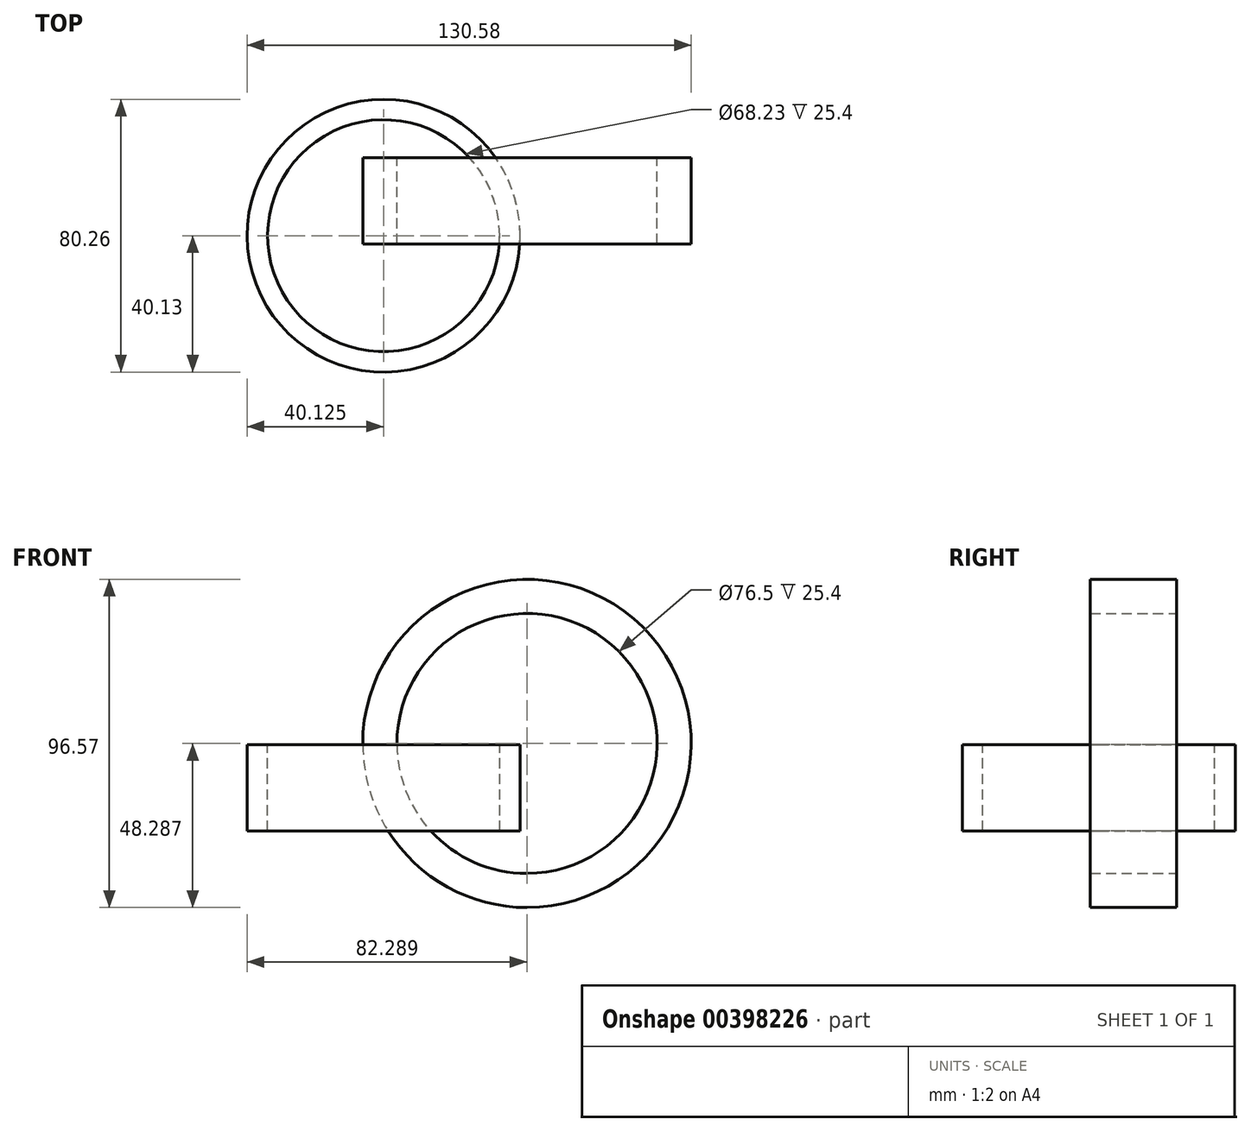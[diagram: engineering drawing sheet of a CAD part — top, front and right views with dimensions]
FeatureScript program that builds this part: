
annotation { "Feature Type Name" : "Feature", "Feature Type Description" : "" }
export const myFeature = defineFeature(function(context is Context, id is Id, definition is map)
    precondition{}
    {
        {
            var Q0;
            Q0=qCreatedBy(makeId("Top.planeOp"),FACE);
            var sketch = newSketch(context, id + "F0", { "sketchPlane" : qUnion([Q0])});
            skCircle(sketch, "E0", {"center": v(-59.1, 59.6) * mm, "radius": 40.13 * mm});
            skSolve(sketch);
        }
        {
            var Q0;
            Q0 = qSketchRegion(id + "F0", true);
            extrude(context, id + "F1", {"entities" : qUnion([Q0]), "depth" : 25.4 * mm});
        }
        {
            var Q0;
            Q0=makeQuery(id+"F1.opExtrude","CAP_FACE",FACE,{"disambiguationData":[OSD([sQuery(id+"F0.wireOp",EDGE,"E0")])],"isStart":false});
            var sketch = newSketch(context, id + "F2", { "sketchPlane" : qUnion([Q0])});
            skCircle(sketch, "E1", {"center": v(-59.1, 59.6) * mm, "radius": 34.12 * mm});
            skSolve(sketch);
        }
        {
            var Q0;
            Q0 = qSketchRegion(id + "F2", true);
            extrude(context, id + "F3", {"entities" : qUnion([Q0]), "operationType" : NewBodyOperationType.REMOVE, "endBound" : BoundingType.THROUGH_ALL, "oppositeDirection" : true, "depth" : 25.4 * mm});
        }
        {
            var Q0;
            Q0=qCreatedBy(makeId("Front.planeOp"),FACE);
            var sketch = newSketch(context, id + "F4", { "sketchPlane" : qUnion([Q0])});
            skCircle(sketch, "E2", {"center": v(-16.94, 25.75) * mm, "radius": 48.29 * mm});
            skCircle(sketch, "E3", {"center": v(-16.94, 25.75) * mm, "radius": 38.25 * mm});
            skSolve(sketch);
        }
        {
            var Q0;
            Q0 = qSketchRegion(id + "F4", true);
            extrude(context, id + "F5", {"entities" : qUnion([Q0]), "depth" : 25.4 * mm});
        }
        {
            var Q0;
            Q0=makeQuery(id+"F5.opExtrude","SWEPT_BODY",BODY,{"disambiguationData":[OSD([sQuery(id+"F4.wireOp",EDGE,"E2"),sQuery(id+"F4.wireOp",EDGE,"E3")])]});
            transform(context, id + "F6", {"entities" : qUnion([Q0]), "transformType" : TransformType.TRANSLATION_3D, "dx" : 0 * mm, "dy" : 82.55 * mm, "dz" : 0 * mm, "makeCopy" : false});
        }
    });
